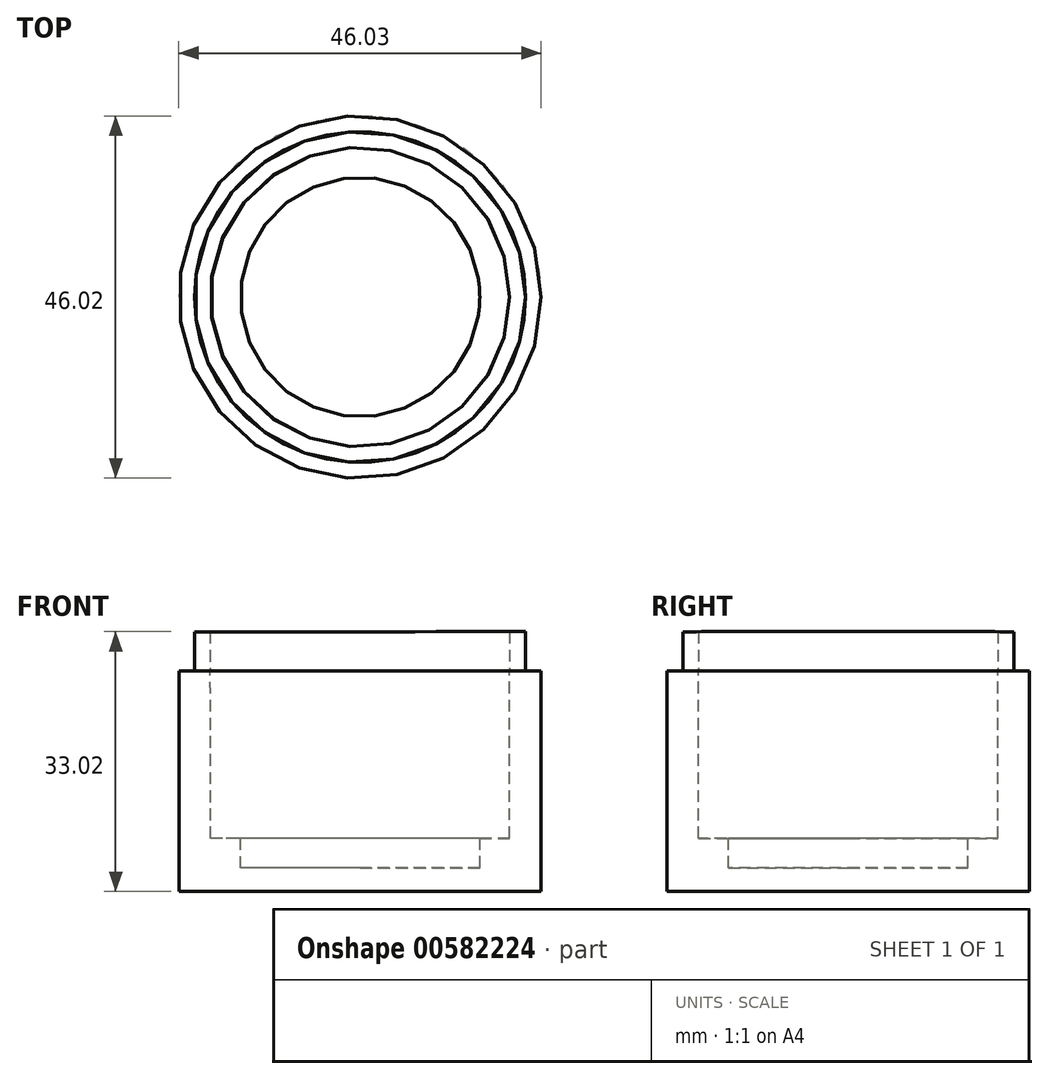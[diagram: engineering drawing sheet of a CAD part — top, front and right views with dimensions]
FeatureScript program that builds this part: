
annotation { "Feature Type Name" : "Feature", "Feature Type Description" : "" }
export const myFeature = defineFeature(function(context is Context, id is Id, definition is map)
    precondition{}
    {
        {
            var Q0;
            Q0=qCreatedBy(makeId("Front.planeOp"),FACE);
            var sketch = newSketch(context, id + "F0", { "sketchPlane" : qUnion([Q0])});
            skLineSegment(sketch, "E0", {"start": v(-20.8, 21.24) * mm, "end": v(-20.8, 26.24) * mm});
            skLineSegment(sketch, "E1", {"start": v(0.23, -3.75) * mm, "end": v(0.23, -6.74) * mm});
            skLineSegment(sketch, "E2", {"start": v(-22.77, -6.76) * mm, "end": v(0.23, -6.74) * mm});
            skLineSegment(sketch, "E3.top", {"start": v(-18.77, 0) * mm, "end": v(-14.97, 0) * mm});
            skLineSegment(sketch, "E3.right", {"start": v(-14.97, -3.76) * mm, "end": v(-14.97, 0) * mm});
            skLineSegment(sketch, "E4", {"start": v(-14.97, -3.76) * mm, "end": v(0.23, -3.75) * mm});
            skLineSegment(sketch, "E5", {"start": v(-18.77, 0) * mm, "end": v(-18.8, 21.25) * mm});
            skLineSegment(sketch, "E6", {"start": v(-18.8, 21.25) * mm, "end": v(-18.8, 26.24) * mm});
            skLineSegment(sketch, "E7", {"start": v(-18.8, 26.24) * mm, "end": v(-20.8, 26.24) * mm});
            skLineSegment(sketch, "E8", {"start": v(-20.8, 21.24) * mm, "end": v(-22.8, 21.24) * mm});
            skLineSegment(sketch, "E9", {"start": v(-22.77, -6.76) * mm, "end": v(-22.8, 21.24) * mm});
            skLineSegment(sketch, "E10.MirrorCS", {"start": v(19.24, 26.26) * mm, "end": v(21.24, 26.26) * mm});
            skLineSegment(sketch, "E11.MirrorCS", {"start": v(21.24, 21.26) * mm, "end": v(23.23, 21.26) * mm});
            skLineSegment(sketch, "E12.MirrorCS", {"start": v(19.23, 0.02) * mm, "end": v(15.43, 0.01) * mm});
            skLineSegment(sketch, "E13.MirrorCS", {"start": v(21.24, 21.26) * mm, "end": v(21.24, 26.26) * mm});
            skLineSegment(sketch, "E14.MirrorCS", {"start": v(19.23, 0.02) * mm, "end": v(19.24, 21.26) * mm});
            skLineSegment(sketch, "E15.MirrorCS", {"start": v(15.43, -3.74) * mm, "end": v(15.43, 0.01) * mm});
            skLineSegment(sketch, "E16.MirrorCS", {"start": v(23.23, -6.74) * mm, "end": v(23.23, 21.26) * mm});
            skLineSegment(sketch, "E17.MirrorCS", {"start": v(19.24, 21.26) * mm, "end": v(19.24, 26.26) * mm});
            skLineSegment(sketch, "E18.MirrorCS", {"start": v(15.43, -3.74) * mm, "end": v(0.23, -3.75) * mm});
            skLineSegment(sketch, "E19.MirrorCS", {"start": v(23.23, -6.74) * mm, "end": v(0.23, -6.74) * mm});
            skSolve(sketch);
        }
        {
            var Q0;
            Q0=makeQuery(id+"F0.imprint","IMPRINT",FACE,{"disambiguationData":[TD([[makeQuery(id+"F0.imprint","IMPRINT",EDGE,{"derivedFrom":sQuery(id+"F0.wireOp",EDGE,"E0")}),-1.0]])]});
            var Q1;
            Q1=sQuery(id+"F0.wireOp",EDGE,"E1");
            revolve(context, id + "F1", {"entities" : qUnion([Q0]), "axis" : qUnion([Q1]), "revolveType" : RevolveType.FULL});
        }
    });
